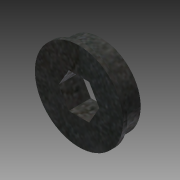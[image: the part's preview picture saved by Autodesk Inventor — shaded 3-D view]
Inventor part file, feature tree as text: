
AUTODESK INVENTOR PART (.ipt)
format: ipt  version: 2014 (Build 180170000, 170)  size: 116,736 bytes
history: native  units: in
note: dims shown in document units (in); Inventor stores cm internally (conversion verified against a paired STEP export)
features: extrude x2, sketch x2
ambient origin geometry x8: Origin, YZ Plane, XZ Plane, XY Plane, X Axis, Y Axis, Z Axis, Center Point
bodies: Solid1 (feature_tree)
feature tree (4):
  extrude  "Extrusion1"  Depth=0.5in
  extrude  "Extrusion2"  Depth=0.0625in
  sketch  "Sketch1"  dims[d0=0.5in d1=1.125in]
  sketch  "Sketch2"  dims[d2=0.25in d3=0.0in d4=0.0625in d5=0.0625in d6=0.0in]
